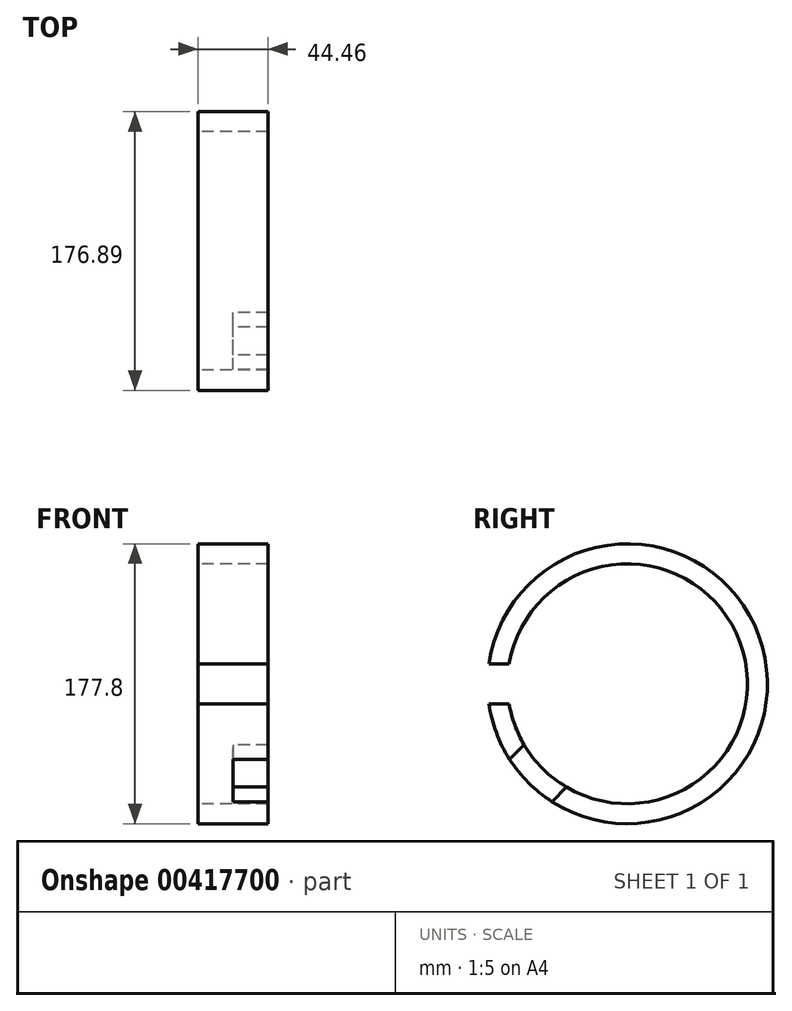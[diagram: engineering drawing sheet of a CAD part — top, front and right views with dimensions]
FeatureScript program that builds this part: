
annotation { "Feature Type Name" : "Feature", "Feature Type Description" : "" }
export const myFeature = defineFeature(function(context is Context, id is Id, definition is map)
    precondition{}
    {
        {
            var Q0;
            Q0=qCreatedBy(makeId("Front.planeOp"),FACE);
            var sketch = newSketch(context, id + "F0", { "sketchPlane" : qUnion([Q0])});
            skLineSegment(sketch, "E0", {"start": v(-22.22, 88.9) * mm, "end": v(-22.22, 76.2) * mm});
            skLineSegment(sketch, "E1", {"start": v(-22.22, 76.2) * mm, "end": v(22.22, 76.2) * mm});
            skLineSegment(sketch, "E2", {"start": v(22.23, 76.2) * mm, "end": v(22.23, 88.9) * mm});
            skLineSegment(sketch, "E3", {"start": v(22.22, 88.9) * mm, "end": v(-22.22, 88.9) * mm});
            skPoint(sketch, "E4", {"position": v(0, 88.9) * mm});
            skLineSegment(sketch, "E5", {"start": v(-22.22, 0) * mm, "end": v(22.22, 0) * mm});
            skSolve(sketch);
        }
        {
            var Q0;
            Q0 = qSketchRegion(id + "F0", true);
            var Q1;
            Q1=sQuery(id+"F0.wireOp",EDGE,"E5");
            revolve(context, id + "F1", {"entities" : qUnion([Q0]), "axis" : qUnion([Q1]), "revolveType" : RevolveType.FULL});
        }
        {
            var Q0;
            Q0=qCreatedBy(makeId("Front.planeOp"),FACE);
            var sketch = newSketch(context, id + "F2", { "sketchPlane" : qUnion([Q0])});
            skLineSegment(sketch, "E6", {"start": v(-31.75, 12.7) * mm, "end": v(31.75, 12.7) * mm});
            skLineSegment(sketch, "E7", {"start": v(31.75, 12.7) * mm, "end": v(31.75, -12.7) * mm});
            skLineSegment(sketch, "E8", {"start": v(31.75, -12.7) * mm, "end": v(-31.75, -12.7) * mm});
            skLineSegment(sketch, "E9", {"start": v(-31.75, -12.7) * mm, "end": v(-31.75, 12.7) * mm});
            skPoint(sketch, "E10", {"position": v(0, -12.7) * mm});
            skLineSegment(sketch, "E11", {"start": v(0, 12.7) * mm, "end": v(0, -12.7) * mm});
            skSolve(sketch);
        }
        {
            var Q0;
            {var subQ0=sQuery(id+"F2.wireOp",EDGE,"E7");Q0=makeQuery(id+"F2.imprint","IMPRINT",FACE,{"disambiguationData":[TD([[makeQuery(id+"F2.imprint","IMPRINT",EDGE,{"derivedFrom":subQ0}),-1.0]])]});}
            var Q1;
            {var subQ0=sQuery(id+"F2.wireOp",EDGE,"E9");Q1=makeQuery(id+"F2.imprint","IMPRINT",FACE,{"disambiguationData":[TD([[makeQuery(id+"F2.imprint","IMPRINT",EDGE,{"derivedFrom":subQ0}),-1.0]])]});}
            extrude(context, id + "F3", {"entities" : qUnion([Q0, Q1]), "operationType" : NewBodyOperationType.REMOVE, "endBound" : BoundingType.THROUGH_ALL, "depth" : 25.4 * mm});
        }
        {
            var Q0;
            Q0=qCreatedBy(makeId("Front.planeOp"),FACE);
            var Q1;
            Q1=qCreatedBy(makeId("Top.planeOp"),FACE);
            cPlane(context, id + "F4", {"entities" : qUnion([Q0, Q1]), "cplaneType" : CPlaneType.MID_PLANE, "offset" : 25.4 * mm, "width" : 152.4 * mm, "height" : 152.4 * mm});
        }
        {
            var Q0;
            Q0=qCreatedBy(id+"F4.planeOp",FACE);
            var sketch = newSketch(context, id + "F5", { "sketchPlane" : qUnion([Q0])});
            skLineSegment(sketch, "E12", {"start": v(0, 19.05) * mm, "end": v(0, -19.05) * mm});
            skLineSegment(sketch, "E13", {"start": v(0, -19.05) * mm, "end": v(22.23, -19.05) * mm});
            skLineSegment(sketch, "E14", {"start": v(22.23, -19.05) * mm, "end": v(22.23, 19.05) * mm});
            skLineSegment(sketch, "E15", {"start": v(22.23, 19.05) * mm, "end": v(0, 19.05) * mm});
            skSolve(sketch);
        }
        {
            var Q0;
            Q0=makeQuery(id+"F5.imprint","IMPRINT",FACE,{"disambiguationData":[TD([[makeQuery(id+"F5.imprint","IMPRINT",EDGE,{"derivedFrom":sQuery(id+"F5.wireOp",EDGE,"E12")}),1.0]])]});
            extrude(context, id + "F6", {"entities" : qUnion([Q0]), "operationType" : NewBodyOperationType.REMOVE, "endBound" : BoundingType.THROUGH_ALL, "depth" : 25.4 * mm});
        }
    });
